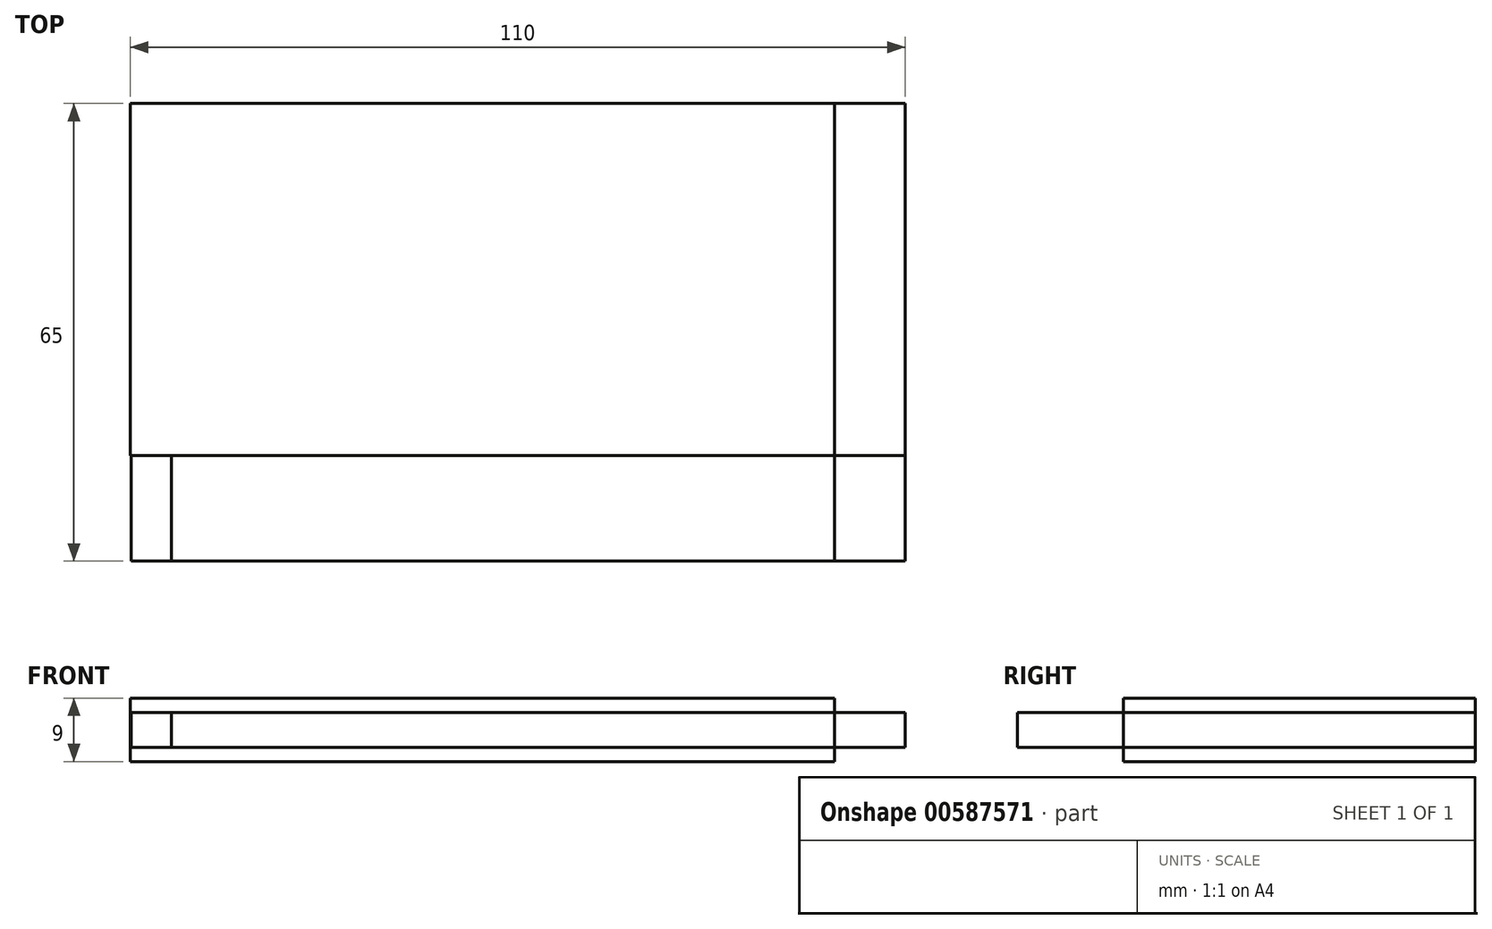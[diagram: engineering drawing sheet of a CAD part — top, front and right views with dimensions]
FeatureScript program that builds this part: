
annotation { "Feature Type Name" : "Feature", "Feature Type Description" : "" }
export const myFeature = defineFeature(function(context is Context, id is Id, definition is map)
    precondition{}
    {
        {
            var Q0;
            Q0=qCreatedBy(makeId("Top.planeOp"),FACE);
            var sketch = newSketch(context, id + "F0", { "sketchPlane" : qUnion([Q0])});
            skLineSegment(sketch, "E0.bottom", {"start": v(0, 0) * mm, "end": v(-100, 0) * mm});
            skLineSegment(sketch, "E0.top", {"start": v(0, 50) * mm, "end": v(-100, 50) * mm});
            skLineSegment(sketch, "E0.left", {"start": v(0, 0) * mm, "end": v(0, 50) * mm});
            skLineSegment(sketch, "E0.right", {"start": v(-100, 0) * mm, "end": v(-100, 50) * mm});
            skSolve(sketch);
        }
        {
            var Q0;
            Q0 = qSketchRegion(id + "F0", true);
            extrude(context, id + "F1", {"entities" : qUnion([Q0]), "depth" : 9 * mm, "offsetDistance" : 25 * mm});
        }
        {
            var Q0;
            Q0=qCreatedBy(makeId("Front.planeOp"),FACE);
            var sketch = newSketch(context, id + "F2", { "sketchPlane" : qUnion([Q0])});
            skLineSegment(sketch, "E1.bottom", {"start": v(-94.2, 9) * mm, "end": v(0, 9) * mm});
            skLineSegment(sketch, "E1.top", {"start": v(-94.2, 0) * mm, "end": v(0, 0) * mm});
            skLineSegment(sketch, "E1.left", {"start": v(-94.2, 9) * mm, "end": v(-94.2, 0) * mm});
            skLineSegment(sketch, "E1.right", {"start": v(0, 9) * mm, "end": v(0, 0) * mm});
            skSolve(sketch);
        }
        {
            var Q0;
            Q0 = qSketchRegion(id + "F2", true);
            extrude(context, id + "F3", {"entities" : qUnion([Q0]), "depth" : 15 * mm, "offsetDistance" : 25 * mm});
        }
        {
            var Q0;
            Q0=makeQuery(id+"F3.opExtrude","SWEPT_FACE",FACE,{"disambiguationData":[OSD([sQuery(id+"F2.wireOp",EDGE,"E1.bottom")])]});
            extrude(context, id + "F4", {"entities" : qUnion([Q0]), "operationType" : NewBodyOperationType.REMOVE, "oppositeDirection" : true, "depth" : 2 * mm, "offsetDistance" : 25 * mm});
        }
        {
            var Q0;
            Q0=makeQuery(id+"F3.opExtrude","SWEPT_FACE",FACE,{"disambiguationData":[OSD([sQuery(id+"F2.wireOp",EDGE,"E1.top")])]});
            extrude(context, id + "F5", {"entities" : qUnion([Q0]), "operationType" : NewBodyOperationType.REMOVE, "oppositeDirection" : true, "depth" : 2 * mm, "offsetDistance" : 25 * mm});
        }
        {
            var Q0;
            Q0=makeQuery(id+"F3.opExtrude","SWEPT_FACE",FACE,{"disambiguationData":[OSD([sQuery(id+"F2.wireOp",EDGE,"E1.right")])]});
            extrude(context, id + "F6", {"entities" : qUnion([Q0]), "depth" : 10 * mm, "offsetDistance" : 25 * mm});
        }
        {
            var Q0;
            {var subQ0=sQuery(id+"F2.wireOp",EDGE,"E1.right");Q0=makeQuery(id+"F6.opExtrude","SWEPT_FACE",FACE,{"disambiguationData":[OSD([subQ0]),TDD([makeQuery(id+"F3.opExtrude","CAP_EDGE",EDGE,{"disambiguationData":[OSD([subQ0])],"isStart":true})])]});}
            extrude(context, id + "F7", {"entities" : qUnion([Q0]), "depth" : 50 * mm, "offsetDistance" : 25 * mm});
        }
        {
            var Q0;
            Q0=makeQuery(id+"F3.opExtrude","SWEPT_FACE",FACE,{"disambiguationData":[OSD([sQuery(id+"F2.wireOp",EDGE,"E1.left")])]});
            extrude(context, id + "F8", {"entities" : qUnion([Q0]), "depth" : 5.7 * mm, "offsetDistance" : 25 * mm});
        }
    });
